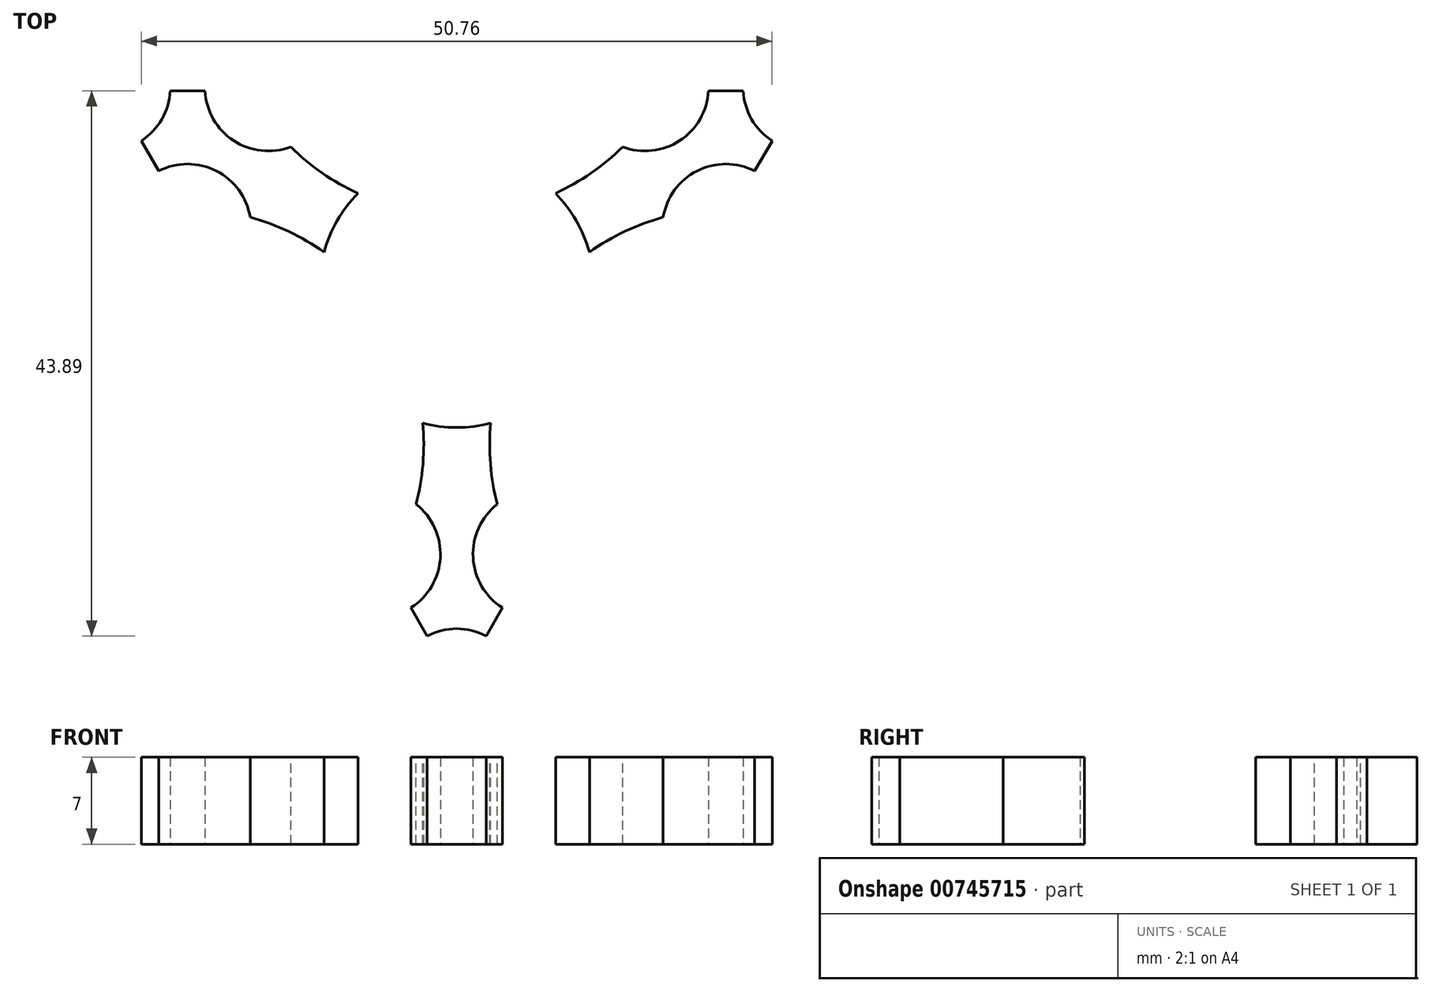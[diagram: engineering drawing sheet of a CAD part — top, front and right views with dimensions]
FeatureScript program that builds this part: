
annotation { "Feature Type Name" : "Feature", "Feature Type Description" : "" }
export const myFeature = defineFeature(function(context is Context, id is Id, definition is map)
    precondition{}
    {
        {
            var Q0;
            Q0=qCreatedBy(makeId("Top.planeOp"),FACE);
            var sketch = newSketch(context, id + "F0", { "sketchPlane" : qUnion([Q0])});
            skCircle(sketch, "E0", {"center": v(0, 0) * mm, "radius": 11.1 * mm});
            skCircle(sketch, "E1", {"center": v(0, -32.4) * mm, "radius": 5.1 * mm});
            skCircle(sketch, "E2.1.0", {"center": v(6.4, -21.3) * mm, "radius": 5.1 * mm});
            skCircle(sketch, "E2.2.0", {"center": v(-6.4, -21.3) * mm, "radius": 5.1 * mm});
            skPoint(sketch, "E2.center", {"position": v(0, -25) * mm});
            skCircle(sketch, "E3.1.1", {"center": v(28.15, 16.25) * mm, "radius": 5.1 * mm});
            skPoint(sketch, "E3.1.2", {"position": v(21.65, 12.5) * mm});
            skCircle(sketch, "E3.1.3", {"center": v(15.16, 16.25) * mm, "radius": 5.1 * mm});
            skCircle(sketch, "E3.1.4", {"center": v(21.65, 5) * mm, "radius": 5.1 * mm});
            skCircle(sketch, "E3.2.1", {"center": v(-28.15, 16.25) * mm, "radius": 5.1 * mm});
            skPoint(sketch, "E3.2.2", {"position": v(-21.65, 12.5) * mm});
            skCircle(sketch, "E3.2.3", {"center": v(-21.65, 5) * mm, "radius": 5.1 * mm});
            skCircle(sketch, "E3.2.4", {"center": v(-15.16, 16.25) * mm, "radius": 5.1 * mm});
            skLineSegment(sketch, "E4", {"start": v(0, 0) * mm, "end": v(0, -37.5) * mm});
            skPoint(sketch, "E5.orphan", {"position": v(0, -45) * mm});
            skPoint(sketch, "E6.orphan", {"position": v(-43.3, 25) * mm});
            skLineSegment(sketch, "E7", {"start": v(0, 0) * mm, "end": v(0, -50) * mm, "construction": true});
            skLineSegment(sketch, "E8", {"start": v(0, 0) * mm, "end": v(-43.3, 25) * mm, "construction": true});
            skLineSegment(sketch, "E9", {"start": v(0, -50) * mm, "end": v(-43.3, 25) * mm});
            skLineSegment(sketch, "E10.1.0", {"start": v(43.3, 25) * mm, "end": v(0, -50) * mm});
            skLineSegment(sketch, "E10.2.0", {"start": v(-43.3, 25) * mm, "end": v(43.3, 25) * mm});
            skSolve(sketch);
        }
        {
            var Q0;
            Q0=makeQuery(id+"F0.imprint","IMPRINT",FACE,{"disambiguationData":[TD([[makeQuery(id+"F0.imprint","IMPRINT",EDGE,{"derivedFrom":sQuery(id+"F0.wireOp",EDGE,"E0")}),-1.0]])]});
            extrude(context, id + "F1", {"entities" : qUnion([Q0]), "depth" : 7 * mm, "offsetDistance" : 25 * mm});
        }
        {
            var Q0;
            Q0=makeQuery(id+"F1.opExtrude","SWEPT_EDGE",EDGE,{"disambiguationData":[OSD([sQuery(id+"F0.wireOp",EDGE,"E9"),sQuery(id+"F0.wireOp",EDGE,"E10.2.0")])]});
            var Q1;
            Q1=makeQuery(id+"F1.opExtrude","SWEPT_EDGE",EDGE,{"disambiguationData":[OSD([sQuery(id+"F0.wireOp",EDGE,"E10.1.0"),sQuery(id+"F0.wireOp",EDGE,"E10.2.0")])]});
            var Q2;
            Q2=makeQuery(id+"F1.opExtrude","SWEPT_EDGE",EDGE,{"disambiguationData":[OSD([sQuery(id+"F0.wireOp",EDGE,"E9"),sQuery(id+"F0.wireOp",EDGE,"E10.1.0")])]});
            fillet(context, id + "F2", {"entities" : qUnion([Q0, Q1, Q2]), "radius" : 5 * mm, "tangentPropagation" : true, "allowEdgeOverflow" : false});
        }
        {
            var Q0;
            Q0=makeQuery(id+"F1.opExtrude","CAP_FACE",FACE,{"disambiguationData":[OSD([sQuery(id+"F0.wireOp",EDGE,"E0"),sQuery(id+"F0.wireOp",EDGE,"E1"),sQuery(id+"F0.wireOp",EDGE,"E2.1.0"),sQuery(id+"F0.wireOp",EDGE,"E2.2.0"),sQuery(id+"F0.wireOp",EDGE,"E3.1.1"),sQuery(id+"F0.wireOp",EDGE,"E3.1.3"),sQuery(id+"F0.wireOp",EDGE,"E3.1.4"),sQuery(id+"F0.wireOp",EDGE,"E3.2.1"),sQuery(id+"F0.wireOp",EDGE,"E3.2.3"),sQuery(id+"F0.wireOp",EDGE,"E3.2.4"),sQuery(id+"F0.wireOp",EDGE,"E9"),sQuery(id+"F0.wireOp",EDGE,"E10.1.0"),sQuery(id+"F0.wireOp",EDGE,"E10.2.0")])],"isStart":false});
            var sketch = newSketch(context, id + "F3", { "sketchPlane" : qUnion([Q0])});
            skCircle(sketch, "E11", {"center": v(0, 25) * mm, "radius": 10 * mm});
            skCircle(sketch, "E12.1.0", {"center": v(-21.65, -12.5) * mm, "radius": 10 * mm});
            skCircle(sketch, "E12.2.0", {"center": v(21.65, -12.5) * mm, "radius": 10 * mm});
            skPoint(sketch, "E12.center", {"position": v(0, 0) * mm});
            skSolve(sketch);
        }
        {
            var Q0;
            {var subQ0=sQuery(id+"F3.wireOp",EDGE,"E11");var subQ1=makeQuery(id+"F1.opExtrude","CAP_EDGE",EDGE,{"disambiguationData":[OSD([sQuery(id+"F0.wireOp",EDGE,"E10.2.0")])],"isStart":false});var subQ2=makeQuery(id+"F3.imprint","INTERSECT",VERTEX,{"disambiguationData":[OD(0.0)],"derivedFrom":[subQ1,subQ0]});Q0=makeQuery(id+"F3.imprint","IMPRINT",FACE,{"disambiguationData":[TD([[makeQuery(id+"F3.imprint","IMPRINT",EDGE,{"disambiguationData":[TD([[subQ2,-1.0]])],"derivedFrom":subQ0}),1.0]])]});}
            var Q1;
            {var subQ0=sQuery(id+"F3.wireOp",EDGE,"E12.1.0");var subQ1=makeQuery(id+"F1.opExtrude","CAP_EDGE",EDGE,{"disambiguationData":[OSD([sQuery(id+"F0.wireOp",EDGE,"E9")])],"isStart":false});var subQ2=makeQuery(id+"F3.imprint","INTERSECT",VERTEX,{"disambiguationData":[OD(0.0)],"derivedFrom":[subQ1,subQ0]});Q1=makeQuery(id+"F3.imprint","IMPRINT",FACE,{"disambiguationData":[TD([[makeQuery(id+"F3.imprint","IMPRINT",EDGE,{"disambiguationData":[TD([[subQ2,-1.0]])],"derivedFrom":subQ0}),1.0]])]});}
            var Q2;
            {var subQ0=sQuery(id+"F3.wireOp",EDGE,"E12.2.0");var subQ1=makeQuery(id+"F1.opExtrude","CAP_EDGE",EDGE,{"disambiguationData":[OSD([sQuery(id+"F0.wireOp",EDGE,"E10.1.0")])],"isStart":false});var subQ2=makeQuery(id+"F3.imprint","INTERSECT",VERTEX,{"disambiguationData":[OD(0.0)],"derivedFrom":[subQ1,subQ0]});Q2=makeQuery(id+"F3.imprint","IMPRINT",FACE,{"disambiguationData":[TD([[makeQuery(id+"F3.imprint","IMPRINT",EDGE,{"disambiguationData":[TD([[subQ2,1.0]])],"derivedFrom":subQ0}),1.0]])]});}
            extrude(context, id + "F4", {"entities" : qUnion([Q0, Q1, Q2]), "operationType" : NewBodyOperationType.REMOVE, "oppositeDirection" : true, "depth" : 25 * mm, "offsetDistance" : 25 * mm});
        }
        {
            var Q0;
            {var subQ0=sQuery(id+"F0.wireOp",EDGE,"E10.1.0");var subQ1=sQuery(id+"F0.wireOp",EDGE,"E9");Q0=makeQuery(id+"F4.boolean.opBoolean","SPLIT",EDGE,{"disambiguationData":[TD([makeQuery(id+"F2.opFillet","BLEND_FACE",FACE,{"disambiguationData":[OSD([subQ1,subQ0])]})])],"derivedFrom":makeQuery(id+"F1.opExtrude","CAP_EDGE",EDGE,{"disambiguationData":[OSD([subQ0])],"isStart":true})});}
            var Q1;
            {var subQ0=sQuery(id+"F0.wireOp",EDGE,"E10.2.0");var subQ1=sQuery(id+"F0.wireOp",EDGE,"E10.1.0");Q1=makeQuery(id+"F4.boolean.opBoolean","SPLIT",EDGE,{"disambiguationData":[TD([makeQuery(id+"F2.opFillet","BLEND_FACE",FACE,{"disambiguationData":[OSD([subQ1,subQ0])]})])],"derivedFrom":makeQuery(id+"F1.opExtrude","CAP_EDGE",EDGE,{"disambiguationData":[OSD([subQ1])],"isStart":true})});}
            var Q2;
            {var subQ0=sQuery(id+"F0.wireOp",EDGE,"E10.2.0");var subQ1=sQuery(id+"F0.wireOp",EDGE,"E9");Q2=makeQuery(id+"F4.boolean.opBoolean","SPLIT",EDGE,{"disambiguationData":[TD([makeQuery(id+"F2.opFillet","BLEND_FACE",FACE,{"disambiguationData":[OSD([subQ1,subQ0])]})])],"derivedFrom":makeQuery(id+"F1.opExtrude","CAP_EDGE",EDGE,{"disambiguationData":[OSD([subQ0])],"isStart":true})});}
            var Q3;
            {var subQ0=sQuery(id+"F0.wireOp",EDGE,"E10.2.0");var subQ1=sQuery(id+"F0.wireOp",EDGE,"E9");Q3=makeQuery(id+"F2.opFillet","BLEND_EDGE",EDGE,{"blendedFrom":[makeQuery(id+"F1.opExtrude","SWEPT_EDGE",EDGE,{"disambiguationData":[OSD([subQ1,subQ0])]}),makeQuery(id+"F1.opExtrude","CAP_FACE",FACE,{"disambiguationData":[OSD([sQuery(id+"F0.wireOp",EDGE,"E0"),sQuery(id+"F0.wireOp",EDGE,"E1"),sQuery(id+"F0.wireOp",EDGE,"E2.1.0"),sQuery(id+"F0.wireOp",EDGE,"E2.2.0"),sQuery(id+"F0.wireOp",EDGE,"E3.1.1"),sQuery(id+"F0.wireOp",EDGE,"E3.1.3"),sQuery(id+"F0.wireOp",EDGE,"E3.1.4"),sQuery(id+"F0.wireOp",EDGE,"E3.2.1"),sQuery(id+"F0.wireOp",EDGE,"E3.2.3"),sQuery(id+"F0.wireOp",EDGE,"E3.2.4"),subQ1,sQuery(id+"F0.wireOp",EDGE,"E10.1.0"),subQ0])],"isStart":false})],"blendedInto":[makeQuery(id+"F1.opExtrude","CAP_FACE",FACE,{"disambiguationData":[OSD([sQuery(id+"F0.wireOp",EDGE,"E0"),sQuery(id+"F0.wireOp",EDGE,"E1"),sQuery(id+"F0.wireOp",EDGE,"E2.1.0"),sQuery(id+"F0.wireOp",EDGE,"E2.2.0"),sQuery(id+"F0.wireOp",EDGE,"E3.1.1"),sQuery(id+"F0.wireOp",EDGE,"E3.1.3"),sQuery(id+"F0.wireOp",EDGE,"E3.1.4"),sQuery(id+"F0.wireOp",EDGE,"E3.2.1"),sQuery(id+"F0.wireOp",EDGE,"E3.2.3"),sQuery(id+"F0.wireOp",EDGE,"E3.2.4"),subQ1,sQuery(id+"F0.wireOp",EDGE,"E10.1.0"),subQ0])],"isStart":false})]});}
            var Q4;
            {var subQ0=sQuery(id+"F0.wireOp",EDGE,"E10.2.0");var subQ1=sQuery(id+"F0.wireOp",EDGE,"E10.1.0");Q4=makeQuery(id+"F2.opFillet","BLEND_EDGE",EDGE,{"blendedFrom":[makeQuery(id+"F1.opExtrude","SWEPT_EDGE",EDGE,{"disambiguationData":[OSD([subQ1,subQ0])]}),makeQuery(id+"F1.opExtrude","CAP_FACE",FACE,{"disambiguationData":[OSD([sQuery(id+"F0.wireOp",EDGE,"E0"),sQuery(id+"F0.wireOp",EDGE,"E1"),sQuery(id+"F0.wireOp",EDGE,"E2.1.0"),sQuery(id+"F0.wireOp",EDGE,"E2.2.0"),sQuery(id+"F0.wireOp",EDGE,"E3.1.1"),sQuery(id+"F0.wireOp",EDGE,"E3.1.3"),sQuery(id+"F0.wireOp",EDGE,"E3.1.4"),sQuery(id+"F0.wireOp",EDGE,"E3.2.1"),sQuery(id+"F0.wireOp",EDGE,"E3.2.3"),sQuery(id+"F0.wireOp",EDGE,"E3.2.4"),sQuery(id+"F0.wireOp",EDGE,"E9"),subQ1,subQ0])],"isStart":false})],"blendedInto":[makeQuery(id+"F1.opExtrude","CAP_FACE",FACE,{"disambiguationData":[OSD([sQuery(id+"F0.wireOp",EDGE,"E0"),sQuery(id+"F0.wireOp",EDGE,"E1"),sQuery(id+"F0.wireOp",EDGE,"E2.1.0"),sQuery(id+"F0.wireOp",EDGE,"E2.2.0"),sQuery(id+"F0.wireOp",EDGE,"E3.1.1"),sQuery(id+"F0.wireOp",EDGE,"E3.1.3"),sQuery(id+"F0.wireOp",EDGE,"E3.1.4"),sQuery(id+"F0.wireOp",EDGE,"E3.2.1"),sQuery(id+"F0.wireOp",EDGE,"E3.2.3"),sQuery(id+"F0.wireOp",EDGE,"E3.2.4"),sQuery(id+"F0.wireOp",EDGE,"E9"),subQ1,subQ0])],"isStart":false})]});}
            var Q5;
            {var subQ0=sQuery(id+"F0.wireOp",EDGE,"E10.1.0");var subQ1=sQuery(id+"F0.wireOp",EDGE,"E9");Q5=makeQuery(id+"F2.opFillet","BLEND_EDGE",EDGE,{"blendedFrom":[makeQuery(id+"F1.opExtrude","SWEPT_EDGE",EDGE,{"disambiguationData":[OSD([subQ1,subQ0])]}),makeQuery(id+"F1.opExtrude","CAP_FACE",FACE,{"disambiguationData":[OSD([sQuery(id+"F0.wireOp",EDGE,"E0"),sQuery(id+"F0.wireOp",EDGE,"E1"),sQuery(id+"F0.wireOp",EDGE,"E2.1.0"),sQuery(id+"F0.wireOp",EDGE,"E2.2.0"),sQuery(id+"F0.wireOp",EDGE,"E3.1.1"),sQuery(id+"F0.wireOp",EDGE,"E3.1.3"),sQuery(id+"F0.wireOp",EDGE,"E3.1.4"),sQuery(id+"F0.wireOp",EDGE,"E3.2.1"),sQuery(id+"F0.wireOp",EDGE,"E3.2.3"),sQuery(id+"F0.wireOp",EDGE,"E3.2.4"),subQ1,subQ0,sQuery(id+"F0.wireOp",EDGE,"E10.2.0")])],"isStart":false})],"blendedInto":[makeQuery(id+"F1.opExtrude","CAP_FACE",FACE,{"disambiguationData":[OSD([sQuery(id+"F0.wireOp",EDGE,"E0"),sQuery(id+"F0.wireOp",EDGE,"E1"),sQuery(id+"F0.wireOp",EDGE,"E2.1.0"),sQuery(id+"F0.wireOp",EDGE,"E2.2.0"),sQuery(id+"F0.wireOp",EDGE,"E3.1.1"),sQuery(id+"F0.wireOp",EDGE,"E3.1.3"),sQuery(id+"F0.wireOp",EDGE,"E3.1.4"),sQuery(id+"F0.wireOp",EDGE,"E3.2.1"),sQuery(id+"F0.wireOp",EDGE,"E3.2.3"),sQuery(id+"F0.wireOp",EDGE,"E3.2.4"),subQ1,subQ0,sQuery(id+"F0.wireOp",EDGE,"E10.2.0")])],"isStart":false})]});}
            fillet(context, id + "F5", {"entities" : qUnion([Q0, Q1, Q2, Q3, Q4, Q5]), "radius" : 2 * mm, "tangentPropagation" : true, "allowEdgeOverflow" : false});
        }
        {
            var Q0;
            Q0=makeQuery(id+"F4.boolean.opBoolean","INTERSECT",EDGE,{"derivedFrom":[makeQuery(id+"F1.opExtrude","CAP_FACE",FACE,{"disambiguationData":[OSD([sQuery(id+"F0.wireOp",EDGE,"E0"),sQuery(id+"F0.wireOp",EDGE,"E1"),sQuery(id+"F0.wireOp",EDGE,"E2.1.0"),sQuery(id+"F0.wireOp",EDGE,"E2.2.0"),sQuery(id+"F0.wireOp",EDGE,"E3.1.1"),sQuery(id+"F0.wireOp",EDGE,"E3.1.3"),sQuery(id+"F0.wireOp",EDGE,"E3.1.4"),sQuery(id+"F0.wireOp",EDGE,"E3.2.1"),sQuery(id+"F0.wireOp",EDGE,"E3.2.3"),sQuery(id+"F0.wireOp",EDGE,"E3.2.4"),sQuery(id+"F0.wireOp",EDGE,"E9"),sQuery(id+"F0.wireOp",EDGE,"E10.1.0"),sQuery(id+"F0.wireOp",EDGE,"E10.2.0")])],"isStart":true}),makeQuery(id+"F4.opExtrude","SWEPT_FACE",FACE,{"disambiguationData":[OSD([sQuery(id+"F3.wireOp",EDGE,"E12.2.0")])]})]});
            var Q1;
            Q1=makeQuery(id+"F4.boolean.opBoolean","INTERSECT",EDGE,{"derivedFrom":[makeQuery(id+"F1.opExtrude","CAP_FACE",FACE,{"disambiguationData":[OSD([sQuery(id+"F0.wireOp",EDGE,"E0"),sQuery(id+"F0.wireOp",EDGE,"E1"),sQuery(id+"F0.wireOp",EDGE,"E2.1.0"),sQuery(id+"F0.wireOp",EDGE,"E2.2.0"),sQuery(id+"F0.wireOp",EDGE,"E3.1.1"),sQuery(id+"F0.wireOp",EDGE,"E3.1.3"),sQuery(id+"F0.wireOp",EDGE,"E3.1.4"),sQuery(id+"F0.wireOp",EDGE,"E3.2.1"),sQuery(id+"F0.wireOp",EDGE,"E3.2.3"),sQuery(id+"F0.wireOp",EDGE,"E3.2.4"),sQuery(id+"F0.wireOp",EDGE,"E9"),sQuery(id+"F0.wireOp",EDGE,"E10.1.0"),sQuery(id+"F0.wireOp",EDGE,"E10.2.0")])],"isStart":true}),makeQuery(id+"F4.opExtrude","SWEPT_FACE",FACE,{"disambiguationData":[OSD([sQuery(id+"F3.wireOp",EDGE,"E12.1.0")])]})]});
            var Q2;
            Q2=makeQuery(id+"F4.boolean.opBoolean","INTERSECT",EDGE,{"derivedFrom":[makeQuery(id+"F1.opExtrude","CAP_FACE",FACE,{"disambiguationData":[OSD([sQuery(id+"F0.wireOp",EDGE,"E0"),sQuery(id+"F0.wireOp",EDGE,"E1"),sQuery(id+"F0.wireOp",EDGE,"E2.1.0"),sQuery(id+"F0.wireOp",EDGE,"E2.2.0"),sQuery(id+"F0.wireOp",EDGE,"E3.1.1"),sQuery(id+"F0.wireOp",EDGE,"E3.1.3"),sQuery(id+"F0.wireOp",EDGE,"E3.1.4"),sQuery(id+"F0.wireOp",EDGE,"E3.2.1"),sQuery(id+"F0.wireOp",EDGE,"E3.2.3"),sQuery(id+"F0.wireOp",EDGE,"E3.2.4"),sQuery(id+"F0.wireOp",EDGE,"E9"),sQuery(id+"F0.wireOp",EDGE,"E10.1.0"),sQuery(id+"F0.wireOp",EDGE,"E10.2.0")])],"isStart":true}),makeQuery(id+"F4.opExtrude","SWEPT_FACE",FACE,{"disambiguationData":[OSD([sQuery(id+"F3.wireOp",EDGE,"E11")])]})]});
            fillet(context, id + "F6", {"entities" : qUnion([Q0, Q1, Q2]), "radius" : 2 * mm, "tangentPropagation" : true, "allowEdgeOverflow" : false});
        }
        {
            var Q0;
            Q0=makeQuery(id+"F1.opExtrude","CAP_FACE",FACE,{"disambiguationData":[OSD([sQuery(id+"F0.wireOp",EDGE,"E0"),sQuery(id+"F0.wireOp",EDGE,"E1"),sQuery(id+"F0.wireOp",EDGE,"E2.1.0"),sQuery(id+"F0.wireOp",EDGE,"E2.2.0"),sQuery(id+"F0.wireOp",EDGE,"E3.1.1"),sQuery(id+"F0.wireOp",EDGE,"E3.1.3"),sQuery(id+"F0.wireOp",EDGE,"E3.1.4"),sQuery(id+"F0.wireOp",EDGE,"E3.2.1"),sQuery(id+"F0.wireOp",EDGE,"E3.2.3"),sQuery(id+"F0.wireOp",EDGE,"E3.2.4"),sQuery(id+"F0.wireOp",EDGE,"E9"),sQuery(id+"F0.wireOp",EDGE,"E10.1.0"),sQuery(id+"F0.wireOp",EDGE,"E10.2.0")])],"isStart":false});
            var sketch = newSketch(context, id + "F7", { "sketchPlane" : qUnion([Q0])});
            skArc(sketch, "E13.0", {"start": v(16.73, 16) * mm, "mid": v(0, 6) * mm, "end": v(-16.73, 16) * mm});
            skLineSegment(sketch, "E13.1", {"start": v(27.71, 16) * mm, "end": v(16.73, 16) * mm});
            skLineSegment(sketch, "E13.2", {"start": v(-16.73, 16) * mm, "end": v(-27.71, 16) * mm});
            skLineSegment(sketch, "E13.3", {"start": v(22.22, 6.5) * mm, "end": v(27.71, 16) * mm});
            skArc(sketch, "E13.4", {"start": v(5.49, -22.5) * mm, "mid": v(5.2, -3) * mm, "end": v(22.22, 6.5) * mm});
            skLineSegment(sketch, "E13.5", {"start": v(-27.71, 16) * mm, "end": v(-22.22, 6.5) * mm});
            skArc(sketch, "E13.6", {"start": v(-22.22, 6.5) * mm, "mid": v(-5.2, -3) * mm, "end": v(-5.49, -22.5) * mm});
            skLineSegment(sketch, "E13.7", {"start": v(-5.49, -22.5) * mm, "end": v(0, -32) * mm});
            skLineSegment(sketch, "E13.8", {"start": v(0, -32) * mm, "end": v(5.49, -22.5) * mm});
            skCircle(sketch, "E14", {"center": v(0, 0) * mm, "radius": 58.67 * mm});
            skSolve(sketch);
        }
        {
            var Q0;
            Q0=qSketchRegion(id+"F7",true);
            extrude(context, id + "F8", {"entities" : qUnion([Q0]), "operationType" : NewBodyOperationType.REMOVE, "oppositeDirection" : true, "depth" : 25 * mm, "offsetDistance" : 25 * mm});
        }
    });
